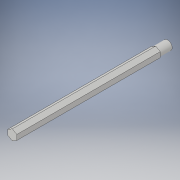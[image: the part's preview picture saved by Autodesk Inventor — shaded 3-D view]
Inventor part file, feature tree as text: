
AUTODESK INVENTOR PART (.ipt)
format: ipt  version: 2018 (Build 220112000, 112)  size: 112,640 bytes
history: native  units: in
note: dims shown in document units (in); Inventor stores cm internally (conversion verified against a paired STEP export)
features: extrude x2, sketch x2
ambient origin geometry x8: Origin, YZ Plane, XZ Plane, XY Plane, X Axis, Y Axis, Z Axis, Center Point
bodies: Solid1 (feature_tree)
feature tree (4):
  extrude  "Extrusion1"  Depth=6.0in
  extrude  "Extrusion3"  [1 undecoded]
  sketch  "Sketch1"  dims[d0=6.0in d1=0.0in d5=0.1875in]
  sketch  "Sketch3"  dims[d13=0.5in d14=0.0in]
note: 1 required parameter value undecoded (feature->parameter linkage not recoverable at this tier; creation-order binding heuristic only, values carry confidence <= 0.55)
